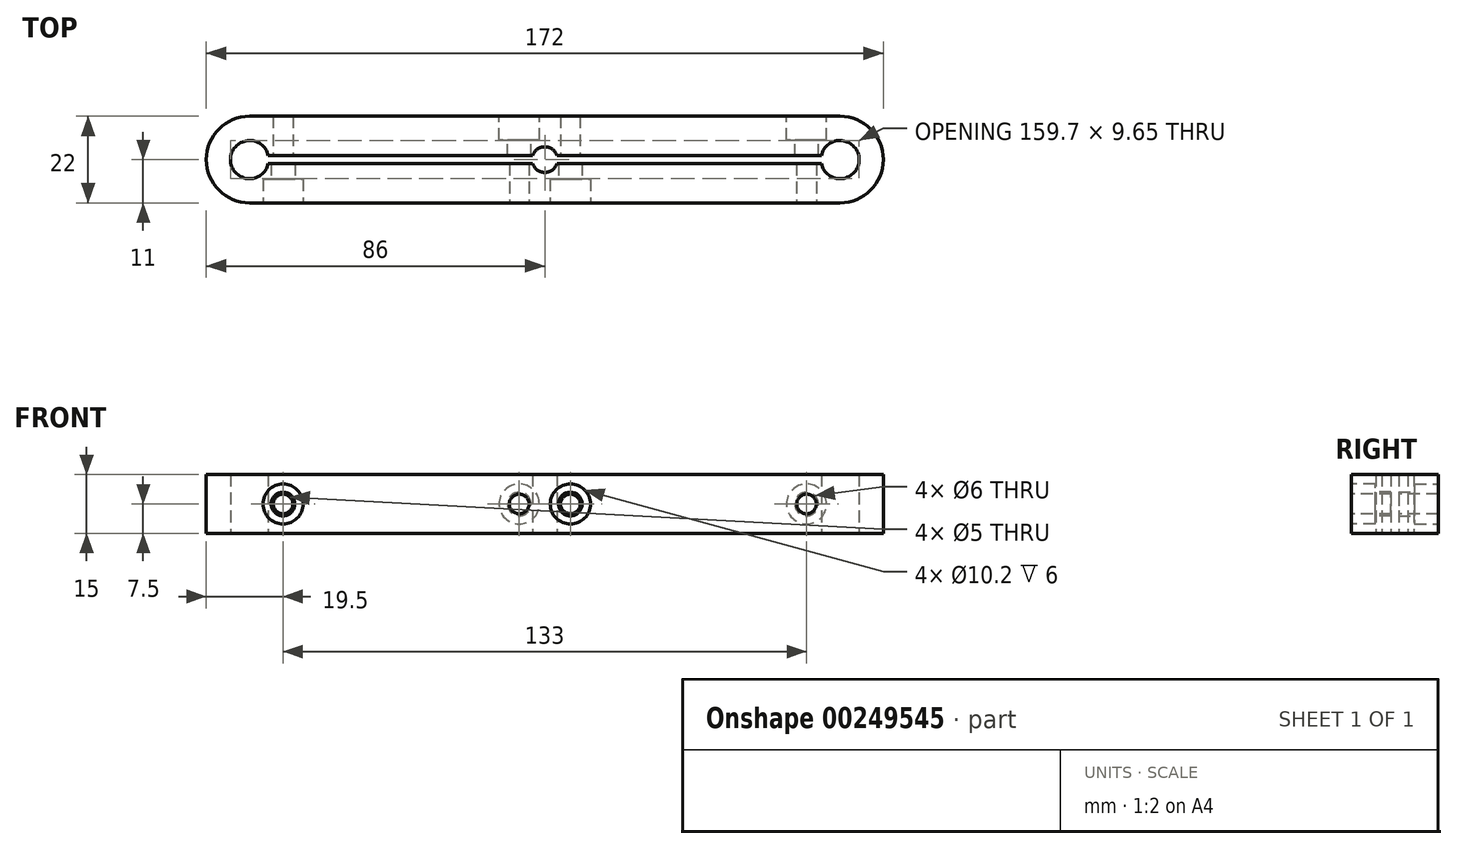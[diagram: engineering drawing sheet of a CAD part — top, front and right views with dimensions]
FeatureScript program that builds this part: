
annotation { "Feature Type Name" : "Feature", "Feature Type Description" : "" }
export const myFeature = defineFeature(function(context is Context, id is Id, definition is map)
    precondition{}
    {
        {
            var Q0;
            Q0=qCreatedBy(makeId("Top.planeOp"),FACE);
            var sketch = newSketch(context, id + "F0", { "sketchPlane" : qUnion([Q0])});
            skCircle(sketch, "E0", {"center": v(0, 0) * mm, "radius": 3.25 * mm});
            skCircle(sketch, "E1", {"center": v(75, 0) * mm, "radius": 4.85 * mm});
            skCircle(sketch, "E2.MirrorC", {"center": v(-75, 0) * mm, "radius": 4.85 * mm});
            skLineSegment(sketch, "E3", {"start": v(0, -11) * mm, "end": v(75, -11) * mm});
            skArc(sketch, "E4", {"start": v(75, -11) * mm, "mid": v(86, 0) * mm, "end": v(75, 11) * mm});
            skLineSegment(sketch, "E5.MirrorCS", {"start": v(0, 11) * mm, "end": v(75, 11) * mm});
            skLineSegment(sketch, "E6.MirrorCS", {"start": v(0, 11) * mm, "end": v(-75, 11) * mm});
            skArc(sketch, "E7.MirrorCS", {"start": v(-75, -11) * mm, "mid": v(-86, 0) * mm, "end": v(-75, 11) * mm});
            skLineSegment(sketch, "E8.MirrorCS", {"start": v(0, -11) * mm, "end": v(-75, -11) * mm});
            skSolve(sketch);
        }
        {
            var Q0;
            Q0 = qSketchRegion(id + "F0", true);
            extrude(context, id + "F1", {"entities" : qUnion([Q0]), "depth" : 15 * mm});
        }
        {
            var Q0;
            Q0=makeQuery(id+"F1.opExtrude","CAP_FACE",FACE,{"disambiguationData":[OSD([sQuery(id+"F0.wireOp",EDGE,"E0"),sQuery(id+"F0.wireOp",EDGE,"E1"),sQuery(id+"F0.wireOp",EDGE,"E2.MirrorC"),sQuery(id+"F0.wireOp",EDGE,"E3"),sQuery(id+"F0.wireOp",EDGE,"E4"),sQuery(id+"F0.wireOp",EDGE,"E5.MirrorCS"),sQuery(id+"F0.wireOp",EDGE,"E6.MirrorCS"),sQuery(id+"F0.wireOp",EDGE,"E7.MirrorCS"),sQuery(id+"F0.wireOp",EDGE,"E8.MirrorCS")])],"isStart":false});
            var sketch = newSketch(context, id + "F2", { "sketchPlane" : qUnion([Q0])});
            skLineSegment(sketch, "E9", {"start": v(75, 1) * mm, "end": v(0, 1) * mm});
            skLineSegment(sketch, "E10.MirrorCS", {"start": v(75, -1) * mm, "end": v(0, -1) * mm});
            skLineSegment(sketch, "E11", {"start": v(75, 1) * mm, "end": v(75, -1) * mm});
            skLineSegment(sketch, "E12.MirrorCS", {"start": v(-75, 1) * mm, "end": v(0, 1) * mm});
            skLineSegment(sketch, "E13.MirrorCS", {"start": v(-75, 1) * mm, "end": v(-75, -1) * mm});
            skLineSegment(sketch, "E14.MirrorCS", {"start": v(-75, -1) * mm, "end": v(0, -1) * mm});
            skSolve(sketch);
        }
        {
            var Q0;
            Q0 = qSketchRegion(id + "F2", true);
            extrude(context, id + "F3", {"entities" : qUnion([Q0]), "operationType" : NewBodyOperationType.REMOVE, "endBound" : BoundingType.THROUGH_ALL, "oppositeDirection" : true, "depth" : 25 * mm});
        }
        {
            var Q0;
            Q0=makeQuery(id+"F1.opExtrude","SWEPT_FACE",FACE,{"disambiguationData":[OSD([sQuery(id+"F0.wireOp",EDGE,"E3"),sQuery(id+"F0.wireOp",EDGE,"E8.MirrorCS")])]});
            var sketch = newSketch(context, id + "F4", { "sketchPlane" : qUnion([Q0])});
            skCircle(sketch, "E15", {"center": v(-66.5, 7.5) * mm, "radius": 2.5 * mm});
            skPoint(sketch, "E15.centerSnap0", {"position": v(-75, 7.5) * mm});
            skCircle(sketch, "E16.MirrorC", {"center": v(66.5, 7.5) * mm, "radius": 2.5 * mm});
            skCircle(sketch, "E17", {"center": v(-6.5, 7.5) * mm, "radius": 2.5 * mm});
            skCircle(sketch, "E18.MirrorC", {"center": v(6.5, 7.5) * mm, "radius": 2.5 * mm});
            skSolve(sketch);
        }
        {
            var Q0;
            Q0 = qSketchRegion(id + "F4", true);
            extrude(context, id + "F5", {"entities" : qUnion([Q0]), "operationType" : NewBodyOperationType.REMOVE, "endBound" : BoundingType.THROUGH_ALL, "oppositeDirection" : true, "depth" : 25 * mm});
        }
        {
            var Q0;
            Q0=makeQuery(id+"F1.opExtrude","SWEPT_FACE",FACE,{"disambiguationData":[OSD([sQuery(id+"F0.wireOp",EDGE,"E3"),sQuery(id+"F0.wireOp",EDGE,"E8.MirrorCS")])]});
            var sketch = newSketch(context, id + "F6", { "sketchPlane" : qUnion([Q0])});
            skCircle(sketch, "E19", {"center": v(-66.5, 7.5) * mm, "radius": 3 * mm});
            skCircle(sketch, "E20", {"center": v(6.5, 7.5) * mm, "radius": 3 * mm});
            skSolve(sketch);
        }
        {
            var Q0;
            Q0 = qSketchRegion(id + "F6", true);
            var Q1;
            {var subQ7=sQuery(id+"F0.wireOp",EDGE,"E2.MirrorC");Q1=makeQuery(id+"F3.boolean.opBoolean","COPY",FACE,{"disambiguationData":[TD([makeQuery(id+"F1.opExtrude","SWEPT_FACE",FACE,{"disambiguationData":[OSD([subQ7])]})])],"derivedFrom":makeQuery(id+"F3.opExtrude","SWEPT_FACE",FACE,{"disambiguationData":[OSD([sQuery(id+"F2.wireOp",EDGE,"E10.MirrorCS"),sQuery(id+"F2.wireOp",EDGE,"E14.MirrorCS")])]})});}
            extrude(context, id + "F7", {"entities" : qUnion([Q0]), "operationType" : NewBodyOperationType.REMOVE, "endBound" : BoundingType.UP_TO_SURFACE, "oppositeDirection" : true, "endBoundEntityFace" : qUnion([Q1]), "depth" : 25 * mm});
        }
        {
            var Q0;
            Q0=makeQuery(id+"F1.opExtrude","SWEPT_FACE",FACE,{"disambiguationData":[OSD([sQuery(id+"F0.wireOp",EDGE,"E5.MirrorCS"),sQuery(id+"F0.wireOp",EDGE,"E6.MirrorCS")])]});
            var sketch = newSketch(context, id + "F8", { "sketchPlane" : qUnion([Q0])});
            skCircle(sketch, "E21", {"center": v(-66.5, 7.5) * mm, "radius": 3 * mm});
            skCircle(sketch, "E22", {"center": v(6.5, 7.5) * mm, "radius": 3 * mm});
            skSolve(sketch);
        }
        {
            var Q0;
            Q0 = qSketchRegion(id + "F8", true);
            var Q1;
            {var subQ8=sQuery(id+"F0.wireOp",EDGE,"E1");Q1=makeQuery(id+"F3.boolean.opBoolean","COPY",FACE,{"disambiguationData":[TD([makeQuery(id+"F1.opExtrude","SWEPT_FACE",FACE,{"disambiguationData":[OSD([subQ8])]})])],"derivedFrom":makeQuery(id+"F3.opExtrude","SWEPT_FACE",FACE,{"disambiguationData":[OSD([sQuery(id+"F2.wireOp",EDGE,"E9"),sQuery(id+"F2.wireOp",EDGE,"E12.MirrorCS")])]})});}
            extrude(context, id + "F9", {"entities" : qUnion([Q0]), "operationType" : NewBodyOperationType.REMOVE, "endBound" : BoundingType.UP_TO_SURFACE, "oppositeDirection" : true, "endBoundEntityFace" : qUnion([Q1]), "depth" : 25 * mm});
        }
        {
            var Q0;
            Q0=makeQuery(id+"F1.opExtrude","SWEPT_FACE",FACE,{"disambiguationData":[OSD([sQuery(id+"F0.wireOp",EDGE,"E5.MirrorCS"),sQuery(id+"F0.wireOp",EDGE,"E6.MirrorCS")])]});
            var sketch = newSketch(context, id + "F10", { "sketchPlane" : qUnion([Q0])});
            skCircle(sketch, "E23", {"center": v(-66.5, 7.5) * mm, "radius": 5.1 * mm});
            skCircle(sketch, "E24", {"center": v(6.5, 7.5) * mm, "radius": 5.1 * mm});
            skSolve(sketch);
        }
        {
            var Q0;
            Q0 = qSketchRegion(id + "F10", true);
            extrude(context, id + "F11", {"entities" : qUnion([Q0]), "operationType" : NewBodyOperationType.REMOVE, "oppositeDirection" : true, "depth" : 6 * mm});
        }
        {
            var Q0;
            Q0=makeQuery(id+"F1.opExtrude","SWEPT_FACE",FACE,{"disambiguationData":[OSD([sQuery(id+"F0.wireOp",EDGE,"E3"),sQuery(id+"F0.wireOp",EDGE,"E8.MirrorCS")])]});
            var sketch = newSketch(context, id + "F12", { "sketchPlane" : qUnion([Q0])});
            skCircle(sketch, "E25", {"center": v(-66.5, 7.5) * mm, "radius": 5.1 * mm});
            skCircle(sketch, "E26", {"center": v(6.5, 7.5) * mm, "radius": 5.1 * mm});
            skSolve(sketch);
        }
        {
            var Q0;
            Q0 = qSketchRegion(id + "F12", true);
            extrude(context, id + "F13", {"entities" : qUnion([Q0]), "operationType" : NewBodyOperationType.REMOVE, "oppositeDirection" : true, "depth" : 6 * mm});
        }
    });
